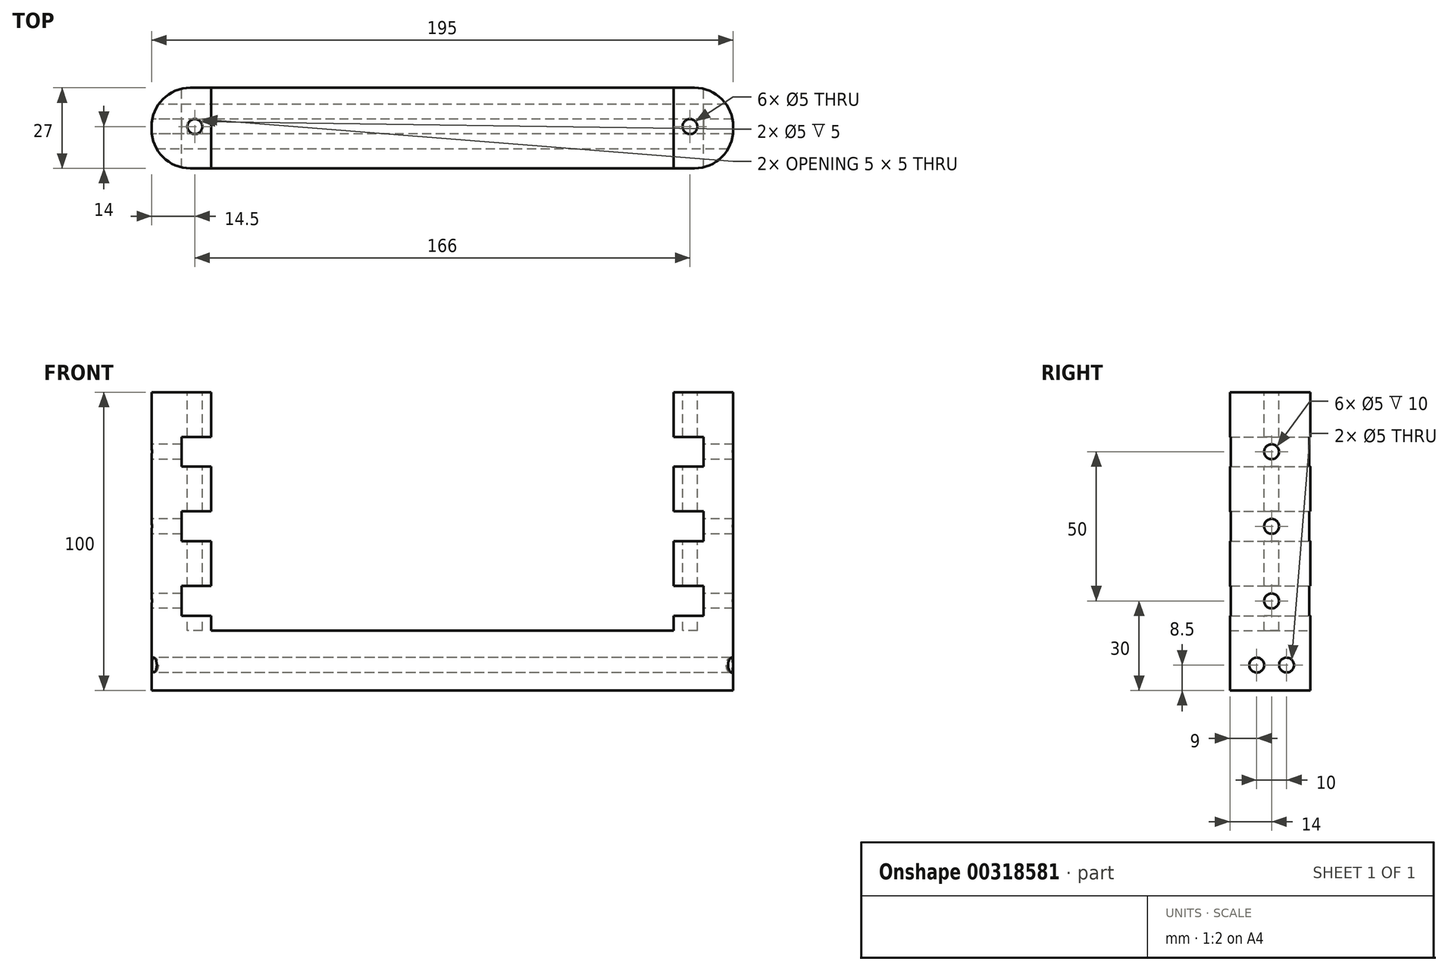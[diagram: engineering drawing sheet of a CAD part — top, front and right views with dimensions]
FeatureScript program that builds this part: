
annotation { "Feature Type Name" : "Feature", "Feature Type Description" : "" }
export const myFeature = defineFeature(function(context is Context, id is Id, definition is map)
    precondition{}
    {
        {
            var Q0;
            Q0=qCreatedBy(makeId("Front.planeOp"),FACE);
            var sketch = newSketch(context, id + "F0", { "sketchPlane" : qUnion([Q0])});
            skLineSegment(sketch, "E0.bottom", {"start": v(0, 0) * mm, "end": v(195, 0) * mm});
            skLineSegment(sketch, "E0.top", {"start": v(0, 100) * mm, "end": v(195, 100) * mm});
            skLineSegment(sketch, "E0.left", {"start": v(0, 0) * mm, "end": v(0, 100) * mm});
            skLineSegment(sketch, "E0.right", {"start": v(195, 0) * mm, "end": v(195, 100) * mm});
            skSolve(sketch);
        }
        {
            var Q0;
            Q0=makeQuery(id+"F0.imprint","IMPRINT",FACE,{"disambiguationData":[TD([[makeQuery(id+"F0.imprint","IMPRINT",EDGE,{"derivedFrom":sQuery(id+"F0.wireOp",EDGE,"E0.bottom")}),1.0]])]});
            extrude(context, id + "F1", {"entities" : qUnion([Q0]), "depth" : 27 * mm});
        }
        {
            var Q0;
            Q0=qCreatedBy(makeId("Front.planeOp"),FACE);
            var sketch = newSketch(context, id + "F2", { "sketchPlane" : qUnion([Q0])});
            skLineSegment(sketch, "E1.bottom", {"start": v(20, 100) * mm, "end": v(175, 100) * mm});
            skLineSegment(sketch, "E1.top", {"start": v(20, 20) * mm, "end": v(175, 20) * mm});
            skLineSegment(sketch, "E1.left", {"start": v(20, 100) * mm, "end": v(20, 20) * mm});
            skLineSegment(sketch, "E1.right", {"start": v(175, 100) * mm, "end": v(175, 20) * mm});
            skSolve(sketch);
        }
        {
            var Q0;
            Q0=makeQuery(id+"F2.imprint","IMPRINT",FACE,{"disambiguationData":[TD([[makeQuery(id+"F2.imprint","IMPRINT",EDGE,{"derivedFrom":sQuery(id+"F2.wireOp",EDGE,"E1.bottom")}),-1.0]])]});
            extrude(context, id + "F3", {"entities" : qUnion([Q0]), "operationType" : NewBodyOperationType.REMOVE, "endBound" : BoundingType.THROUGH_ALL, "depth" : 25 * mm});
        }
        {
            var Q0;
            Q0=qCreatedBy(makeId("Front.planeOp"),FACE);
            var sketch = newSketch(context, id + "F4", { "sketchPlane" : qUnion([Q0])});
            skLineSegment(sketch, "E2.bottom", {"start": v(185, 85) * mm, "end": v(175, 85) * mm});
            skLineSegment(sketch, "E2.top", {"start": v(185, 75) * mm, "end": v(175, 75) * mm});
            skLineSegment(sketch, "E2.left", {"start": v(185, 85) * mm, "end": v(185, 75) * mm});
            skLineSegment(sketch, "E2.right", {"start": v(175, 85) * mm, "end": v(175, 75) * mm});
            skLineSegment(sketch, "E3.bottom", {"start": v(185, 60) * mm, "end": v(175, 60) * mm});
            skLineSegment(sketch, "E3.top", {"start": v(185, 50) * mm, "end": v(175, 50) * mm});
            skLineSegment(sketch, "E3.left", {"start": v(185, 60) * mm, "end": v(185, 50) * mm});
            skLineSegment(sketch, "E3.right", {"start": v(175, 60) * mm, "end": v(175, 50) * mm});
            skLineSegment(sketch, "E4.bottom", {"start": v(185, 35) * mm, "end": v(175, 35) * mm});
            skLineSegment(sketch, "E4.top", {"start": v(185, 25) * mm, "end": v(175, 25) * mm});
            skLineSegment(sketch, "E4.left", {"start": v(185, 35) * mm, "end": v(185, 25) * mm});
            skLineSegment(sketch, "E4.right", {"start": v(175, 35) * mm, "end": v(175, 25) * mm});
            skLineSegment(sketch, "E5.bottom", {"start": v(20, 85) * mm, "end": v(10, 85) * mm});
            skLineSegment(sketch, "E5.top", {"start": v(20, 75) * mm, "end": v(10, 75) * mm});
            skLineSegment(sketch, "E5.left", {"start": v(20, 85) * mm, "end": v(20, 75) * mm});
            skLineSegment(sketch, "E5.right", {"start": v(10, 85) * mm, "end": v(10, 75) * mm});
            skLineSegment(sketch, "E6.bottom", {"start": v(20, 60) * mm, "end": v(10, 60) * mm});
            skLineSegment(sketch, "E6.top", {"start": v(20, 50) * mm, "end": v(10, 50) * mm});
            skLineSegment(sketch, "E6.left", {"start": v(20, 60) * mm, "end": v(20, 50) * mm});
            skLineSegment(sketch, "E6.right", {"start": v(10, 60) * mm, "end": v(10, 50) * mm});
            skLineSegment(sketch, "E7.bottom", {"start": v(20, 35) * mm, "end": v(10, 35) * mm});
            skLineSegment(sketch, "E7.top", {"start": v(20, 25) * mm, "end": v(10, 25) * mm});
            skLineSegment(sketch, "E7.left", {"start": v(20, 35) * mm, "end": v(20, 25) * mm});
            skLineSegment(sketch, "E7.right", {"start": v(10, 35) * mm, "end": v(10, 25) * mm});
            skLineSegment(sketch, "E8", {"start": v(185, 100) * mm, "end": v(185, 40) * mm, "construction": true});
            skLineSegment(sketch, "E9", {"start": v(10, 100) * mm, "end": v(10, 85) * mm, "construction": true});
            skSolve(sketch);
        }
        {
            var Q0;
            Q0=makeQuery(id+"F4.imprint","IMPRINT",FACE,{"disambiguationData":[TD([[makeQuery(id+"F4.imprint","IMPRINT",EDGE,{"derivedFrom":sQuery(id+"F4.wireOp",EDGE,"E2.bottom")}),1.0]])]});
            var Q1;
            Q1=makeQuery(id+"F4.imprint","IMPRINT",FACE,{"disambiguationData":[TD([[makeQuery(id+"F4.imprint","IMPRINT",EDGE,{"derivedFrom":sQuery(id+"F4.wireOp",EDGE,"E3.bottom")}),1.0]])]});
            var Q2;
            Q2=makeQuery(id+"F4.imprint","IMPRINT",FACE,{"disambiguationData":[TD([[makeQuery(id+"F4.imprint","IMPRINT",EDGE,{"derivedFrom":sQuery(id+"F4.wireOp",EDGE,"E4.bottom")}),1.0]])]});
            var Q3;
            Q3=makeQuery(id+"F4.imprint","IMPRINT",FACE,{"disambiguationData":[TD([[makeQuery(id+"F4.imprint","IMPRINT",EDGE,{"derivedFrom":sQuery(id+"F4.wireOp",EDGE,"E7.bottom")}),1.0]])]});
            var Q4;
            Q4=makeQuery(id+"F4.imprint","IMPRINT",FACE,{"disambiguationData":[TD([[makeQuery(id+"F4.imprint","IMPRINT",EDGE,{"derivedFrom":sQuery(id+"F4.wireOp",EDGE,"E6.bottom")}),1.0]])]});
            var Q5;
            Q5=makeQuery(id+"F4.imprint","IMPRINT",FACE,{"disambiguationData":[TD([[makeQuery(id+"F4.imprint","IMPRINT",EDGE,{"derivedFrom":sQuery(id+"F4.wireOp",EDGE,"E5.bottom")}),1.0]])]});
            extrude(context, id + "F5", {"entities" : qUnion([Q0, Q1, Q2, Q3, Q4, Q5]), "operationType" : NewBodyOperationType.REMOVE, "endBound" : BoundingType.THROUGH_ALL, "depth" : 25 * mm});
        }
        {
            var Q0;
            {var subQ0=sQuery(id+"F0.wireOp",EDGE,"E0.right");var subQ2=sQuery(id+"F0.wireOp",EDGE,"E0.top");Q0=makeQuery(id+"F3.boolean.opBoolean","SPLIT",FACE,{"disambiguationData":[TD([makeQuery(id+"F1.opExtrude","SWEPT_FACE",FACE,{"disambiguationData":[OSD([subQ0])]})])],"derivedFrom":makeQuery(id+"F1.opExtrude","SWEPT_FACE",FACE,{"disambiguationData":[OSD([subQ2])]})});}
            var sketch = newSketch(context, id + "F6", { "sketchPlane" : qUnion([Q0])});
            skCircle(sketch, "E10", {"center": v(180.5, -13) * mm, "radius": 2.5 * mm});
            skCircle(sketch, "E11", {"center": v(14.5, -13) * mm, "radius": 2.5 * mm});
            skLineSegment(sketch, "E12", {"start": v(97.5, 0) * mm, "end": v(97.5, -27) * mm, "construction": true});
            skSolve(sketch);
        }
        {
            var Q0;
            Q0=makeQuery(id+"F6.imprint","IMPRINT",FACE,{"disambiguationData":[TD([[makeQuery(id+"F6.imprint","IMPRINT",EDGE,{"derivedFrom":sQuery(id+"F6.wireOp",EDGE,"E10")}),1.0]])]});
            var Q1;
            Q1=makeQuery(id+"F6.imprint","IMPRINT",FACE,{"disambiguationData":[TD([[makeQuery(id+"F6.imprint","IMPRINT",EDGE,{"derivedFrom":sQuery(id+"F6.wireOp",EDGE,"E11")}),1.0]])]});
            extrude(context, id + "F7", {"entities" : qUnion([Q0, Q1]), "operationType" : NewBodyOperationType.REMOVE, "oppositeDirection" : true, "depth" : 80 * mm});
        }
        {
            var Q0;
            Q0=qCreatedBy(makeId("Right.planeOp"),FACE);
            var sketch = newSketch(context, id + "F8", { "sketchPlane" : qUnion([Q0])});
            skCircle(sketch, "E13", {"center": v(-13, 80) * mm, "radius": 2.5 * mm});
            skCircle(sketch, "E14", {"center": v(-13, 55) * mm, "radius": 2.5 * mm});
            skCircle(sketch, "E15", {"center": v(-13, 30) * mm, "radius": 2.5 * mm});
            skLineSegment(sketch, "E16", {"start": v(-27, 30) * mm, "end": v(0, 30) * mm, "construction": true});
            skLineSegment(sketch, "E17", {"start": v(-27, 55) * mm, "end": v(0, 55) * mm, "construction": true});
            skLineSegment(sketch, "E18", {"start": v(-13, 0) * mm, "end": v(-13, 100) * mm});
            skSolve(sketch);
        }
        {
            var Q0;
            Q0=makeQuery(id+"F8.imprint","IMPRINT",FACE,{"disambiguationData":[TD([[makeQuery(id+"F8.imprint","IMPRINT",EDGE,{"derivedFrom":sQuery(id+"F8.wireOp",EDGE,"E13")}),1.0]])]});
            var Q1;
            Q1=makeQuery(id+"F8.imprint","IMPRINT",FACE,{"disambiguationData":[TD([[makeQuery(id+"F8.imprint","IMPRINT",EDGE,{"derivedFrom":sQuery(id+"F8.wireOp",EDGE,"E14")}),1.0]])]});
            var Q2;
            Q2=makeQuery(id+"F8.imprint","IMPRINT",FACE,{"disambiguationData":[TD([[makeQuery(id+"F8.imprint","IMPRINT",EDGE,{"derivedFrom":sQuery(id+"F8.wireOp",EDGE,"E15")}),1.0]])]});
            extrude(context, id + "F9", {"entities" : qUnion([Q0, Q1, Q2]), "operationType" : NewBodyOperationType.REMOVE, "endBound" : BoundingType.THROUGH_ALL, "depth" : 25 * mm});
        }
        {
            var Q0;
            Q0=qCreatedBy(makeId("Right.planeOp"),FACE);
            var sketch = newSketch(context, id + "F10", { "sketchPlane" : qUnion([Q0])});
            skCircle(sketch, "E19", {"center": v(-8, 8.5) * mm, "radius": 2.5 * mm});
            skCircle(sketch, "E20", {"center": v(-18, 8.5) * mm, "radius": 2.5 * mm});
            skSolve(sketch);
        }
        {
            var Q0;
            Q0=makeQuery(id+"F10.imprint","IMPRINT",FACE,{"disambiguationData":[TD([[makeQuery(id+"F10.imprint","IMPRINT",EDGE,{"derivedFrom":sQuery(id+"F10.wireOp",EDGE,"E19")}),1.0]])]});
            var Q1;
            Q1=makeQuery(id+"F10.imprint","IMPRINT",FACE,{"disambiguationData":[TD([[makeQuery(id+"F10.imprint","IMPRINT",EDGE,{"derivedFrom":sQuery(id+"F10.wireOp",EDGE,"E20")}),1.0]])]});
            extrude(context, id + "F11", {"entities" : qUnion([Q0, Q1]), "operationType" : NewBodyOperationType.REMOVE, "endBound" : BoundingType.THROUGH_ALL, "depth" : 25 * mm});
        }
        {
            var Q0;
            Q0=makeQuery(id+"F1.opExtrude","CAP_EDGE",EDGE,{"disambiguationData":[OSD([sQuery(id+"F0.wireOp",EDGE,"E0.left")])],"isStart":true});
            var Q1;
            Q1=makeQuery(id+"F1.opExtrude","CAP_EDGE",EDGE,{"disambiguationData":[OSD([sQuery(id+"F0.wireOp",EDGE,"E0.left")])],"isStart":false});
            var Q2;
            Q2=makeQuery(id+"F1.opExtrude","CAP_EDGE",EDGE,{"disambiguationData":[OSD([sQuery(id+"F0.wireOp",EDGE,"E0.right")])],"isStart":false});
            var Q3;
            Q3=makeQuery(id+"F1.opExtrude","CAP_EDGE",EDGE,{"disambiguationData":[OSD([sQuery(id+"F0.wireOp",EDGE,"E0.right")])],"isStart":true});
            fillet(context, id + "F12", {"entities" : qUnion([Q0, Q1, Q2, Q3]), "radius" : 13 * mm, "tangentPropagation" : true, "allowEdgeOverflow" : false});
        }
    });
